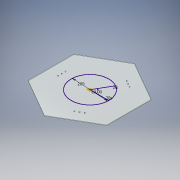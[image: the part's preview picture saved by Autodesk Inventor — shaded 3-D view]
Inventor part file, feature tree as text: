
AUTODESK INVENTOR PART (.ipt)
format: ipt  version: 2019 (Build 230136000, 136)  size: 177,664 bytes
history: native  units: mm
features: plane x2, extrude x2, sketch x2, pattern_circular x1
ambient origin geometry x8: Origin, YZ Plane, XZ Plane, XY Plane, X Axis, Y Axis, Z Axis, Center Point
bodies: Body1 (feature_tree)
feature tree (7):
  plane  "Work Plane2"
  plane  "Work Plane1"
  extrude  "Extrusion8"  Depth=37.5mm
  extrude  "Extrusion10"  Depth=3.0mm
  pattern_circular  "Circular Pattern2"  Count=2  [1 undecoded]
  sketch  "Sketch5"  dims[d2=150.0deg d3=160.0mm d4=20.0mm d5=4.5mm d6=20.0mm d8=20.0mm d9=20.0mm d11=20.0mm d14=10.0mm d15=10.0mm d16=60.0mm d17=40.0mm d18=30.0mm d20=360.0deg d22=96.0mm d45=45.0mm d46=120.0deg d47=50.0mm d48=90.0deg d49=50.0mm d50=30.0deg d51=30.0mm d53=360.0deg d72=125.0mm d77=3.0mm d78=0.0mm d79=150.0mm d80=5.0mm d81=19.995mm d82=5.0mm d83=19.995mm d84=5.0mm d90=5.0mm d91=3.0mm d92=0.0mm d93=30.0mm d94=360.0deg d96=200.0mm d97=20.0mm d98=60.0deg d99=20.0mm]
  sketch  "Sketch4"  dims[d0=75.0mm d1=37.5mm]
note: 1 required parameter value undecoded (feature->parameter linkage not recoverable at this tier; creation-order binding heuristic only, values carry confidence <= 0.55)
